# Revit family: IS_Connect_Multiproduct_BIM_IT_E7719;E7720
name_source: partatom
category: Plumbing Fixtures
revit_build: Autodesk Revit MEP 2014 (Build: 20130308_1515(x64)
units: mm (PartAtom-declared; Revit-internal decimal feet)

## types (2) — shared parameters
Accessori = www.idealstandard.it
AltezzaNominale = 348 mm
Assembly Code = C1030200
Autore = Ideal Standard Italia
Brand = Ideal Standard
Caratteristiche = Vaso sospeso a cacciata con scarico a parete e fissaggi completamente nascosti, completo di sedile slim a sgancio rapido. Per il fissaggio a parete è necessario utilizzare l’apposito kit TT0299327 incluso nella confezione ed il sostegno metallico T655067 da ordinare separatamente. Certificato per scarico 4,5/3 litri.
Colore = Bianco
Connessione = Installazione
Default Elevation = 400 mm  [stored 1.31234 ft]
DescrizioneClassifcazioneUni2015 = WC pans
Dimensione = 349 x 540 x 363 mm
DurataGaranziaProdotti = 99
Finitura = Bianco
Garanzia = Garanzia Idealstandard
IfcEsportaCome = IfcSanitaryTerminalType
InformaziniGaranzia = www.idealstandard.it/garanzia.html
InformazioniDiProdotto = www.idealstandard.it/prodotti/html
InformazioniGaranzia = www.idealstandard.it/garanzia.html
InstruzioniInstallazione = www.idealstandard.it/prodotti/html
LarghezzaNominale = 362 mm
LunghezzaNominale = 540 mm
Materiale = Porcellana Vetrificata (Vitreous China)
NBSDescription = WC pans
NBSReference = 45-30-70/384
PesoNetto = 24,00 KG
Produttore = www.idealstandard.it
ProfonditàNominale = 540 mm
Revisione = 1
RiferimentoClassificazioneUni2015 = Pr_40_20_93_94
Spazio = interno
Telefono = 800 652 290
TipoEspotazioneIfc = WCPANS
URL = www.idealstandard.it
UnitàDurata = anni
UnitàDurataGaranzia = anni
UnitàVolume = Litri
VersioneClassificazioneUni2015 = Products v1.1
zero-valued in all types: CWFU, Cost, CostoDiSostituzione, HWFU, SpilloverLivello, WFU

## per-type parameters (varying)
| type | CodiceABarre | Description | Model | Nome | NomeOggettoBim | NumeroDiModello | e7723 | e7724 |
| E771901 - CONNECT WHG BWL HO WHITE HF RS & SEAT | 5017830474753 | CONNECT WHG BWL HO WHITE HF RS & SEAT | E771901 | WcPans_CONNECT_E771901_IdealStandard | ISI_IdealStandard_WcPans_CONNECT_E771901 | E771901 | Yes | No |
| E772001 - CONNECT WHG BWL HO WHITE HF RS & SC SEAT | 5017830474760 | CONNECT WHG BWL HO WHITE HF RS & SC SEAT | E772001 | WcPans_CONNECT_E772001_IdealStandard | ISI_IdealStandard_WcPans_CONNECT_E772001 | E772001 | No | Yes |

note: [stored X ft] marks values corroborated as IEEE doubles in the binary element streams (Revit-internal decimal feet)

## geometry (parser evidence)
native form markers: Sweep x8
no freeform markers — native parametric forms only
